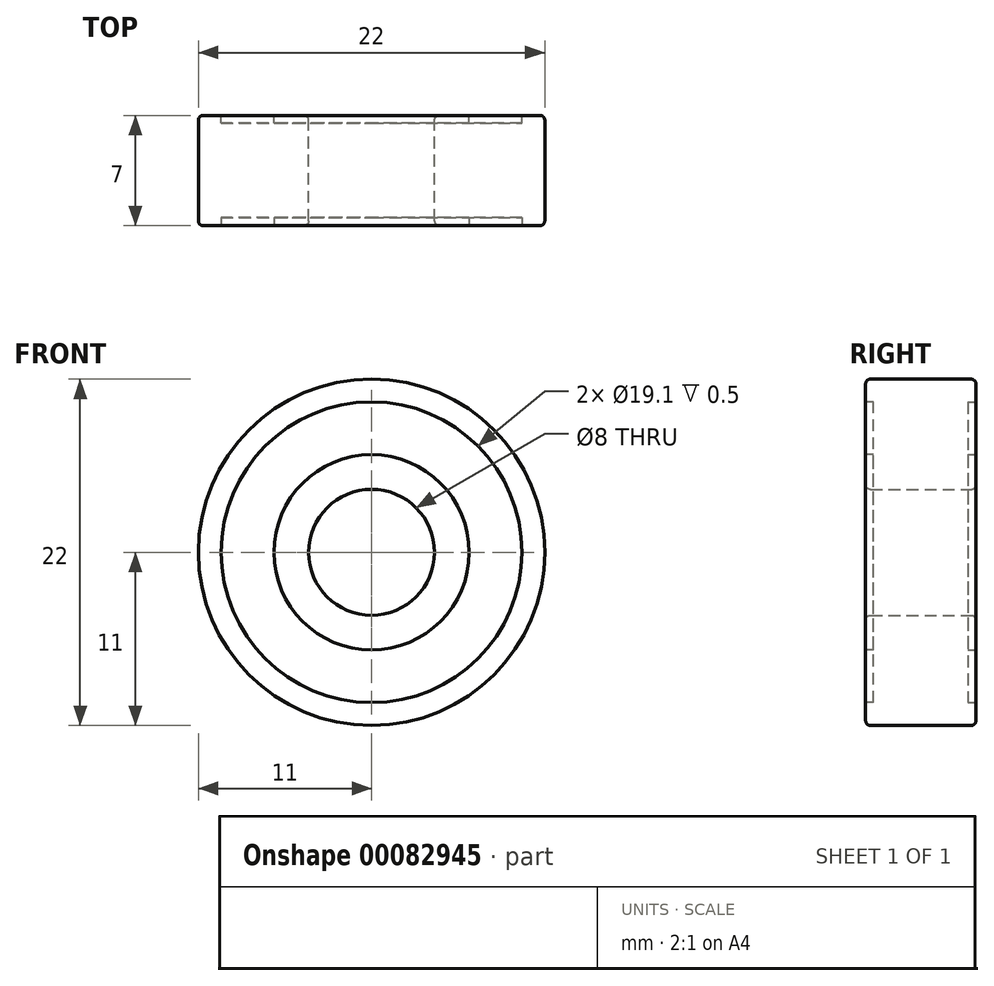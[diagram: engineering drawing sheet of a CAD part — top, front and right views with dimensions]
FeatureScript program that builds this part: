
annotation { "Feature Type Name" : "Feature", "Feature Type Description" : "" }
export const myFeature = defineFeature(function(context is Context, id is Id, definition is map)
    precondition{}
    {
        {
            var Q0;
            Q0=qCreatedBy(makeId("Front.planeOp"),FACE);
            var sketch = newSketch(context, id + "F0", { "sketchPlane" : qUnion([Q0])});
            skCircle(sketch, "E0", {"center": v(0, 0) * mm, "radius": 4 * mm});
            skCircle(sketch, "E1", {"center": v(0, 0) * mm, "radius": 11 * mm});
            skSolve(sketch);
        }
        {
            var Q0;
            Q0=makeQuery(id+"F0.imprint","IMPRINT",FACE,{"disambiguationData":[TD([[makeQuery(id+"F0.imprint","IMPRINT",EDGE,{"derivedFrom":sQuery(id+"F0.wireOp",EDGE,"E0")}),-1.0]])]});
            extrude(context, id + "F1", {"entities" : qUnion([Q0]), "depth" : 7 * mm});
        }
        {
            var Q0;
            Q0=makeQuery(id+"F1.opExtrude","CAP_FACE",FACE,{"disambiguationData":[OSD([sQuery(id+"F0.wireOp",EDGE,"E0"),sQuery(id+"F0.wireOp",EDGE,"E1")])],"isStart":false});
            var sketch = newSketch(context, id + "F2", { "sketchPlane" : qUnion([Q0])});
            skCircle(sketch, "E2", {"center": v(0, 0) * mm, "radius": 6.2 * mm});
            skCircle(sketch, "E3", {"center": v(0, 0) * mm, "radius": 9.55 * mm});
            skSolve(sketch);
        }
        {
            var Q0;
            Q0=makeQuery(id+"F2.imprint","IMPRINT",FACE,{"disambiguationData":[TD([[makeQuery(id+"F2.imprint","IMPRINT",EDGE,{"derivedFrom":sQuery(id+"F2.wireOp",EDGE,"E2")}),-1.0]])]});
            extrude(context, id + "F3", {"entities" : qUnion([Q0]), "operationType" : NewBodyOperationType.REMOVE, "oppositeDirection" : true, "depth" : .5 * mm});
        }
        {
            var Q0;
            Q0=makeQuery(id+"F1.opExtrude","CAP_FACE",FACE,{"disambiguationData":[OSD([sQuery(id+"F0.wireOp",EDGE,"E0"),sQuery(id+"F0.wireOp",EDGE,"E1")])],"isStart":true});
            var sketch = newSketch(context, id + "F4", { "sketchPlane" : qUnion([Q0])});
            skCircle(sketch, "E4", {"center": v(0, 0) * mm, "radius": 6.2 * mm});
            skCircle(sketch, "E5", {"center": v(0, 0) * mm, "radius": 9.55 * mm});
            skSolve(sketch);
        }
        {
            var Q0;
            Q0=makeQuery(id+"F4.imprint","IMPRINT",FACE,{"disambiguationData":[TD([[makeQuery(id+"F4.imprint","IMPRINT",EDGE,{"derivedFrom":sQuery(id+"F4.wireOp",EDGE,"E4")}),-1.0]])]});
            extrude(context, id + "F5", {"entities" : qUnion([Q0]), "operationType" : NewBodyOperationType.REMOVE, "oppositeDirection" : true, "depth" : .5 * mm});
        }
        {
            var Q0;
            Q0=makeQuery(id+"F1.opExtrude","CAP_EDGE",EDGE,{"disambiguationData":[OSD([sQuery(id+"F0.wireOp",EDGE,"E1")])],"isStart":true});
            fillet(context, id + "F6", {"entities" : qUnion([Q0]), "radius" : .3 * mm, "tangentPropagation" : true, "allowEdgeOverflow" : false});
        }
        {
            var Q0;
            Q0=makeQuery(id+"F1.opExtrude","CAP_EDGE",EDGE,{"disambiguationData":[OSD([sQuery(id+"F0.wireOp",EDGE,"E1")])],"isStart":false});
            var Q1;
            Q1=makeQuery(id+"F1.opExtrude","CAP_EDGE",EDGE,{"disambiguationData":[OSD([sQuery(id+"F0.wireOp",EDGE,"E0")])],"isStart":false});
            fillet(context, id + "F7", {"entities" : qUnion([Q0, Q1]), "radius" : 0.3 * mm, "tangentPropagation" : true, "allowEdgeOverflow" : false});
        }
        {
            var Q0;
            Q0=makeQuery(id+"F1.opExtrude","CAP_EDGE",EDGE,{"disambiguationData":[OSD([sQuery(id+"F0.wireOp",EDGE,"E0")])],"isStart":true});
            fillet(context, id + "F8", {"entities" : qUnion([Q0]), "radius" : 0.3 * mm, "tangentPropagation" : true, "allowEdgeOverflow" : false});
        }
    });
